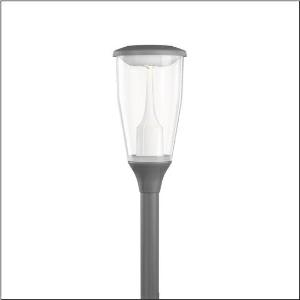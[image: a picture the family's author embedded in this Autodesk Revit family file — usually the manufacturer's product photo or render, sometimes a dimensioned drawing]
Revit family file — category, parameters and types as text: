
# Revit family: dl_11_iq___p1_0a_5xa5575lf14hp00022_ff57
name_source: partatom
category: Lighting Fixtures
units: mm (PartAtom-declared; Revit-internal decimal feet)

## family parameters
Cut with Voids When Loaded = No
Host = Face
Light Source = No
Part Type = Normal
Room Calculation Point = No
Round Connector Dimension = Use Diameter
Shared = No

## types (1)
- --- (1 x LED, 4990 lm, 33.6 W, 4000K)
    Apparent Load = 34 VA
    CIE Flux Codes = 23 60 93 95 100
    Color Rendering = 70
    Color Temperature = 4000K
    Default Elevation = 1800 mm
    Description = DL 11 iQ, mast luminaire, Module 540 iQ-SR, primary light control with 3 zone facetted reflector, of plastic, silver coated, highly specular, structured, primary optical cover: cover, of PMMA, transparent, light distribution: P1.0a, light emission: direct distribution, primary light characteristic: asymmetric, installation type: post-top, LED, High Power LED, light colour: 740, colour temperature: 4000K, control: Street-Remote, Auto-Match, Temp-Guard, Lumen-Switch, Night-Set, Smart-Wire, Light-Fading, Desk-Remote (wireless, voltage-free reading and setting of iQ features in the workshop via application-optimized NFC function/RFID function), optimised constant luminous flux control (CLO 2.0), mains connection: 220..240V, AC, 50/60Hz, connection cable pre-assembled, cable length: 5,5m, wiring characteristics: H07RN-F, 5-core, 1.5mm², start of lifetime: 34W, end of service life: 36W, luminaire housing, upper part, of diecast aluminium, coated, Siteco® metallic grey (DB 702S), spigot size: 76mm (post-top), post-top mast mounting element, of diecast aluminium, coated, Siteco® metallic grey (DB 702S), Module 540 iQ-SR, traffic white (RAL 9016), equipment: Power, protection rating (complete): IP66, insulation class (complete): insulation class II (safety insulation), certification: CE, ENEC, ENEC+, VDE, packaging unit: 1 piece

Light Distribution: P1.0a
    Height = 665 mm
    Lamp = 1 x LED
    Lamp Light Flux = 4990 lm
    Lamp Power = 33.6 W
    Lamp count = 1
    Length = 334 mm
    Luminous efficacy = 149 lm/W
    Manufacturer = Siteco
    ModVariant = No
    Model = 5XA5575LF14HP00022
    Number of Poles = 1
    OnlyDefault = Yes
    Power Factor = 1
    Product Name = DL 11 iQ | P1.0a
    Product group = mast luminaire | pylon top
    ProductGroupID = 6100
    Protection Class = Protection class II
    Protection Degree = IP 66
    RLX_Detail_Level = 1
    RLX_Emergency_Light_Flux = 0 lm
    RLX_Emergency_Type = 0
    RLX_Emergency_Type_DB = No
    RlxData = <blob elided: 108841 chars, md5=cef082f2>
    Socket = socket
    Standby Power = 0 W
    System Light Flux = 4990 lm
    System Power = 34 W
    Type Comments = factory setting: luminous flux: 100 % | dim-lin: 254 | 695 mA
    Type Image = l_1258354.jpg
    URL = http://relux.com
    VarID = @adj_021783
    Voltage = 0 V
    Weight = 0.00 kg
    Width = 0 mm  [stored 0 ft]

note: [stored X ft] marks values corroborated as IEEE doubles in the binary element streams (Revit-internal decimal feet)

## geometry (parser evidence)
native form markers: Blend x4, Sweep x11
no freeform markers — native parametric forms only
